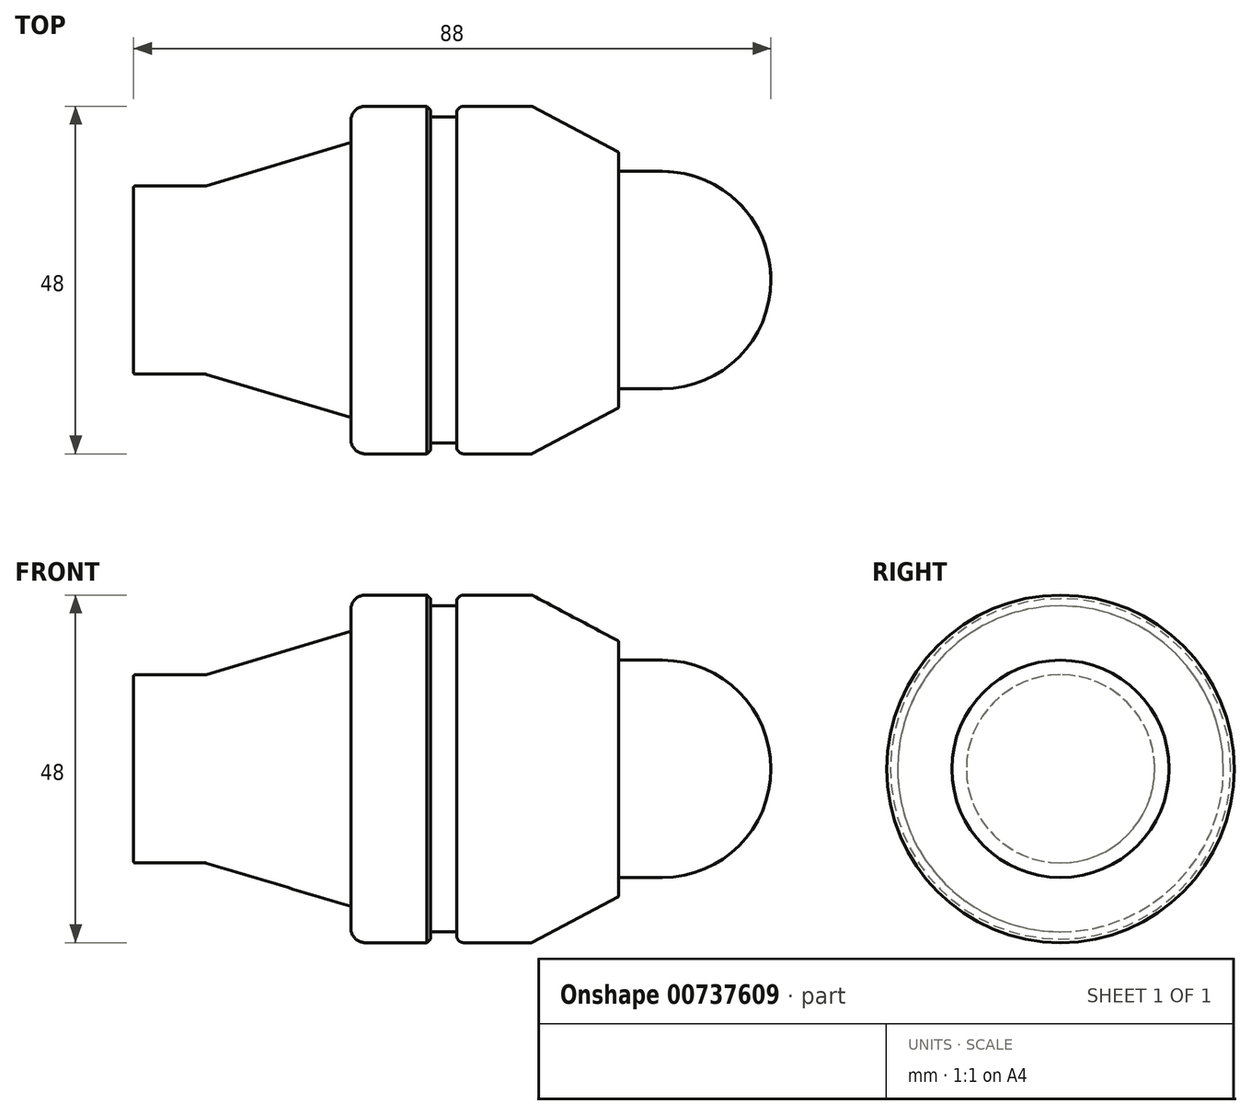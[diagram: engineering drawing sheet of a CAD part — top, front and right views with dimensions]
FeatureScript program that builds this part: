
annotation { "Feature Type Name" : "Feature", "Feature Type Description" : "" }
export const myFeature = defineFeature(function(context is Context, id is Id, definition is map)
    precondition{}
    {
        {
            var Q0;
            Q0=qCreatedBy(makeId("Top.planeOp"),FACE);
            var sketch = newSketch(context, id + "F0", { "sketchPlane" : qUnion([Q0])});
            skArc(sketch, "E0", {"start": v(15, 0) * mm, "mid": v(10.6, 10.6) * mm, "end": v(0, 15) * mm});
            skLineSegment(sketch, "E1", {"start": v(0, 15) * mm, "end": v(-6, 15) * mm});
            skLineSegment(sketch, "E2", {"start": v(-6, 15) * mm, "end": v(-6, 17.62) * mm});
            skLineSegment(sketch, "E3", {"start": v(-18, 24) * mm, "end": v(-6, 17.62) * mm});
            skLineSegment(sketch, "E4", {"start": v(-18, 24) * mm, "end": v(-28.4, 24) * mm});
            skLineSegment(sketch, "E5", {"start": v(-28.4, 24) * mm, "end": v(-28.4, 22.5) * mm});
            skLineSegment(sketch, "E6", {"start": v(-28.4, 22.5) * mm, "end": v(-32, 22.5) * mm});
            skLineSegment(sketch, "E7", {"start": v(-32, 22.5) * mm, "end": v(-32, 24) * mm});
            skLineSegment(sketch, "E8", {"start": v(-32, 24) * mm, "end": v(-43, 24) * mm});
            skLineSegment(sketch, "E9", {"start": v(-43, 24) * mm, "end": v(-43, 19) * mm});
            skLineSegment(sketch, "E10", {"start": v(-43, 19) * mm, "end": v(-63, 13) * mm});
            skLineSegment(sketch, "E11", {"start": v(-63, 13) * mm, "end": v(-73, 13) * mm});
            skLineSegment(sketch, "E12", {"start": v(-73, 13) * mm, "end": v(-73, 0) * mm});
            skLineSegment(sketch, "E13", {"start": v(-73, 0) * mm, "end": v(0, 0) * mm});
            skLineSegment(sketch, "E14", {"start": v(0, 0) * mm, "end": v(15, 0) * mm});
            skLineSegment(sketch, "E15", {"start": v(15, 0) * mm, "end": v(21.63, 6.64) * mm});
            skSolve(sketch);
        }
        {
            var Q0;
            Q0=makeQuery(id+"F0.imprint","IMPRINT",FACE,{"disambiguationData":[TD([[makeQuery(id+"F0.imprint","IMPRINT",EDGE,{"derivedFrom":sQuery(id+"F0.wireOp",EDGE,"E0")}),1.0]])]});
            var Q1;
            Q1=sQuery(id+"F0.wireOp",EDGE,"E13");
            revolve(context, id + "F1", {"surfaceOperationType" : NewSurfaceOperationType.NEW, "entities" : qUnion([Q0]), "axis" : qUnion([Q1]), "revolveType" : RevolveType.FULL});
        }
        {
            var Q0;
            Q0=makeQuery(id+"F1.opRevolve","SWEPT_EDGE",EDGE,{"disambiguationData":[OSD([sQuery(id+"F0.wireOp",EDGE,"E8"),sQuery(id+"F0.wireOp",EDGE,"E9")])]});
            fillet(context, id + "F2", {"entities" : qUnion([Q0]), "radius" : 2 * mm, "tangentPropagation" : true, "allowEdgeOverflow" : false});
        }
        {
            var Q0;
            Q0=makeQuery(id+"F1.opRevolve","SWEPT_EDGE",EDGE,{"disambiguationData":[OSD([sQuery(id+"F0.wireOp",EDGE,"E4"),sQuery(id+"F0.wireOp",EDGE,"E5")])]});
            fillet(context, id + "F3", {"entities" : qUnion([Q0]), "radius" : 1 * mm, "tangentPropagation" : true, "allowEdgeOverflow" : false});
        }
        {
            var Q0;
            Q0=makeQuery(id+"F1.opRevolve","SWEPT_EDGE",EDGE,{"disambiguationData":[OSD([sQuery(id+"F0.wireOp",EDGE,"E7"),sQuery(id+"F0.wireOp",EDGE,"E8")])]});
            chamfer(context, id + "F4", {"entities" : qUnion([Q0]), "width" : 0.5 * mm, "tangentPropagation" : true});
        }
        {
            var Q0;
            Q0=makeQuery(id+"F1.opRevolve","SWEPT_EDGE",EDGE,{"disambiguationData":[OSD([sQuery(id+"F0.wireOp",EDGE,"E11"),sQuery(id+"F0.wireOp",EDGE,"E12")])]});
            var Q1;
            Q1=makeQuery(id+"F1.opRevolve","SWEPT_EDGE",EDGE,{"disambiguationData":[OSD([sQuery(id+"F0.wireOp",EDGE,"E10"),sQuery(id+"F0.wireOp",EDGE,"E11")])]});
            var Q2;
            Q2=makeQuery(id+"F1.opRevolve","SWEPT_EDGE",EDGE,{"disambiguationData":[OSD([sQuery(id+"F0.wireOp",EDGE,"E3"),sQuery(id+"F0.wireOp",EDGE,"E4")])]});
            var Q3;
            Q3=makeQuery(id+"F1.opRevolve","SWEPT_EDGE",EDGE,{"disambiguationData":[OSD([sQuery(id+"F0.wireOp",EDGE,"E2"),sQuery(id+"F0.wireOp",EDGE,"E3")])]});
            fillet(context, id + "F5", {"entities" : qUnion([Q0, Q1, Q2, Q3]), "radius" : 0.2 * mm, "tangentPropagation" : true, "allowEdgeOverflow" : false});
        }
        {
            var Q0;
            Q0=makeQuery(id+"F1.opRevolve","SWEPT_EDGE",EDGE,{"disambiguationData":[OSD([sQuery(id+"F0.wireOp",EDGE,"E1"),sQuery(id+"F0.wireOp",EDGE,"E2")])]});
            var Q1;
            Q1=makeQuery(id+"F1.opRevolve","SWEPT_EDGE",EDGE,{"disambiguationData":[OSD([sQuery(id+"F0.wireOp",EDGE,"E0"),sQuery(id+"F0.wireOp",EDGE,"E1")])]});
            var Q2;
            Q2=makeQuery(id+"F1.opRevolve","SWEPT_EDGE",EDGE,{"disambiguationData":[OSD([sQuery(id+"F0.wireOp",EDGE,"E6"),sQuery(id+"F0.wireOp",EDGE,"E7")])]});
            var Q3;
            Q3=makeQuery(id+"F1.opRevolve","SWEPT_FACE",FACE,{"disambiguationData":[OSD([sQuery(id+"F0.wireOp",EDGE,"E6")])]});
            var Q4;
            Q4=makeQuery(id+"F1.opRevolve","SWEPT_EDGE",EDGE,{"disambiguationData":[OSD([sQuery(id+"F0.wireOp",EDGE,"E9"),sQuery(id+"F0.wireOp",EDGE,"E10")])]});
            fillet(context, id + "F6", {"entities" : qUnion([Q0, Q1, Q2, Q3, Q4]), "radius" : 0.2 * mm, "tangentPropagation" : true, "allowEdgeOverflow" : false});
        }
    });
